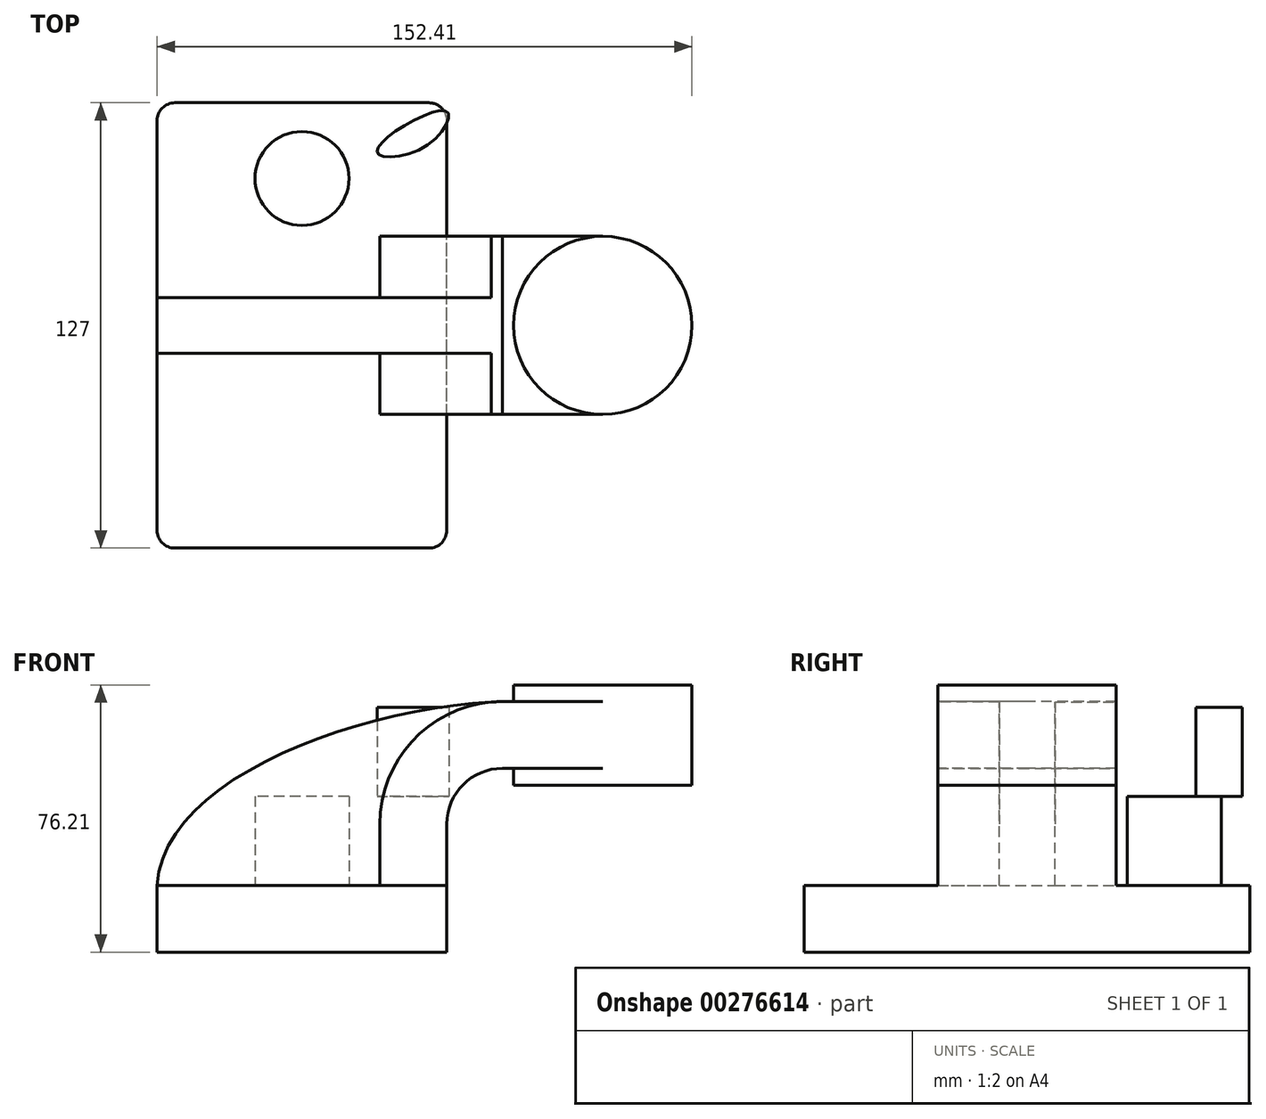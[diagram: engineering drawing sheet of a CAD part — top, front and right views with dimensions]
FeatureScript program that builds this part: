
annotation { "Feature Type Name" : "Feature", "Feature Type Description" : "" }
export const myFeature = defineFeature(function(context is Context, id is Id, definition is map)
    precondition{}
    {
        {
            var Q0;
            Q0=qCreatedBy(makeId("Front.planeOp"),FACE);
            var sketch = newSketch(context, id + "F0", { "sketchPlane" : qUnion([Q0])});
            skLineSegment(sketch, "E0.rect.bottom", {"start": v(-41.28, 9.52) * mm, "end": v(41.28, 9.52) * mm});
            skLineSegment(sketch, "E0.rect.top", {"start": v(-41.28, -9.52) * mm, "end": v(41.28, -9.52) * mm});
            skLineSegment(sketch, "E0.rect.left", {"start": v(-41.28, 9.52) * mm, "end": v(-41.28, -9.52) * mm});
            skLineSegment(sketch, "E0.rect.right", {"start": v(41.28, 9.52) * mm, "end": v(41.28, -9.52) * mm});
            skPoint(sketch, "E0.rect.middle", {"position": v(0, 0) * mm});
            skLineSegment(sketch, "E1", {"start": v(41.28, 9.52) * mm, "end": v(41.28, 27) * mm});
            skArc(sketch, "E2", {"start": v(41.28, 27) * mm, "mid": v(45.92, 38.23) * mm, "end": v(57.15, 42.88) * mm});
            skLineSegment(sketch, "E3", {"start": v(57.15, 42.88) * mm, "end": v(85.72, 42.88) * mm});
            skLineSegment(sketch, "E4.rect.bottom", {"start": v(60.32, 38.1) * mm, "end": v(111.12, 38.1) * mm});
            skLineSegment(sketch, "E4.rect.top", {"start": v(60.32, 66.68) * mm, "end": v(111.12, 66.68) * mm});
            skLineSegment(sketch, "E4.rect.left", {"start": v(60.32, 38.1) * mm, "end": v(60.32, 66.68) * mm});
            skLineSegment(sketch, "E4.rect.right", {"start": v(111.13, 38.1) * mm, "end": v(111.12, 66.68) * mm});
            skPoint(sketch, "E4.rect.middle", {"position": v(85.72, 52.39) * mm});
            skLineSegment(sketch, "E5.0", {"start": v(57.15, 61.93) * mm, "end": v(85.72, 61.93) * mm});
            skArc(sketch, "E5.1", {"start": v(22.23, 27) * mm, "mid": v(32.45, 51.7) * mm, "end": v(57.15, 61.93) * mm});
            skLineSegment(sketch, "E5.2", {"start": v(22.23, 9.52) * mm, "end": v(22.23, 27) * mm});
            skLineSegment(sketch, "E6", {"start": v(85.72, 38.1) * mm, "end": v(85.72, 66.68) * mm});
            skFitSpline(sketch, "E7", {"points": [v(-41.28, 9.53) * mm, v(57.15, 61.93) * mm], "startDerivative": vector(5.2, 92.34) * mm, "endDerivative": vector(120.92, 4.22) * mm});
            skSolve(sketch);
        }
        {
            var Q0;
            Q0=makeQuery(id+"F0.imprint","IMPRINT",FACE,{"disambiguationData":[TD([[makeQuery(id+"F0.imprint","IMPRINT",EDGE,{"derivedFrom":sQuery(id+"F0.wireOp",EDGE,"E0.rect.top")}),1.0]])]});
            extrude(context, id + "F1", {"entities" : qUnion([Q0]), "endBound" : BoundingType.SYMMETRIC, "depth" : 127 * mm});
        }
        {
            var Q0;
            {var subQ9=sQuery(id+"F0.wireOp",EDGE,"E1");Q0=makeQuery(id+"F0.imprint","IMPRINT",FACE,{"disambiguationData":[TD([[makeQuery(id+"F0.imprint","IMPRINT",EDGE,{"derivedFrom":subQ9}),1.0]])]});}
            var Q1;
            {var subQ0=sQuery(id+"F0.wireOp",EDGE,"E6");var subQ1=sQuery(id+"F0.wireOp",EDGE,"E3");var subQ2=makeQuery(id+"F0.imprint","INTERSECT",VERTEX,{"derivedFrom":[subQ1,subQ0]});Q1=makeQuery(id+"F0.imprint","IMPRINT",FACE,{"disambiguationData":[TD([[makeQuery(id+"F0.imprint","IMPRINT",EDGE,{"disambiguationData":[TD([[subQ2,1.0]])],"derivedFrom":subQ1}),1.0]])]});}
            extrude(context, id + "F2", {"entities" : qUnion([Q0, Q1]), "operationType" : NewBodyOperationType.ADD, "endBound" : BoundingType.SYMMETRIC, "depth" : 50.8 * mm});
        }
        {
            var Q0;
            {var subQ3=sQuery(id+"F0.wireOp",EDGE,"E5.2");Q0=makeQuery(id+"F0.imprint","IMPRINT",FACE,{"disambiguationData":[TD([[makeQuery(id+"F0.imprint","IMPRINT",EDGE,{"derivedFrom":subQ3}),1.0]])]});}
            extrude(context, id + "F3", {"entities" : qUnion([Q0]), "operationType" : NewBodyOperationType.ADD, "endBound" : BoundingType.SYMMETRIC, "depth" : 15.88 * mm});
        }
        {
            var Q0;
            {var subQ5=sQuery(id+"F0.wireOp",EDGE,"E4.rect.right");Q0=makeQuery(id+"F0.imprint","IMPRINT",FACE,{"disambiguationData":[TD([[makeQuery(id+"F0.imprint","IMPRINT",EDGE,{"derivedFrom":subQ5}),1.0]])]});}
            var Q1;
            Q1=sQuery(id+"F0.wireOp",EDGE,"E6");
            revolve(context, id + "F4", {"operationType" : NewBodyOperationType.ADD, "entities" : qUnion([Q0]), "axis" : qUnion([Q1]), "revolveType" : RevolveType.FULL});
        }
        {
            var Q0;
            Q0=makeQuery(id+"F1.opExtrude","CAP_EDGE",EDGE,{"disambiguationData":[OSD([sQuery(id+"F0.wireOp",EDGE,"E0.rect.right")])],"isStart":false});
            var Q1;
            Q1=makeQuery(id+"F1.opExtrude","CAP_EDGE",EDGE,{"disambiguationData":[OSD([sQuery(id+"F0.wireOp",EDGE,"E0.rect.left")])],"isStart":false});
            var Q2;
            Q2=makeQuery(id+"F1.opExtrude","CAP_EDGE",EDGE,{"disambiguationData":[OSD([sQuery(id+"F0.wireOp",EDGE,"E0.rect.right")])],"isStart":true});
            var Q3;
            Q3=makeQuery(id+"F1.opExtrude","CAP_EDGE",EDGE,{"disambiguationData":[OSD([sQuery(id+"F0.wireOp",EDGE,"E0.rect.left")])],"isStart":true});
            fillet(context, id + "F5", {"entities" : qUnion([Q0, Q1, Q2, Q3]), "radius" : 5.08 * mm, "tangentPropagation" : true, "allowEdgeOverflow" : false});
        }
        {
            var Q0;
            {var subQ4=sQuery(id+"F0.wireOp",EDGE,"E0.rect.bottom");var subQ5=sQuery(id+"F0.wireOp",EDGE,"E0.rect.right");var subQ6=sQuery(id+"F0.wireOp",EDGE,"E0.rect.left");Q0=makeQuery(id+"F3.boolean.opBoolean","SPLIT",FACE,{"disambiguationData":[TD([makeQuery(id+"F1.opExtrude","CAP_FACE",FACE,{"disambiguationData":[OSD([subQ4,sQuery(id+"F0.wireOp",EDGE,"E0.rect.top"),subQ6,subQ5])],"isStart":true})])],"derivedFrom":makeQuery(id+"F1.opExtrude","SWEPT_FACE",FACE,{"disambiguationData":[OSD([subQ4])]})});}
            var sketch = newSketch(context, id + "F6", { "sketchPlane" : qUnion([Q0])});
            skCircle(sketch, "E8", {"center": v(0, 41.91) * mm, "radius": 13.38 * mm});
            skPoint(sketch, "E8.centerSnap0", {"position": v(41.28, 41.91) * mm});
            skSolve(sketch);
        }
        {
            var Q0;
            Q0=makeQuery(id+"F6.imprint","IMPRINT",FACE,{"disambiguationData":[TD([[makeQuery(id+"F6.imprint","IMPRINT",EDGE,{"derivedFrom":sQuery(id+"F6.wireOp",EDGE,"E8")}),1.0]])]});
            extrude(context, id + "F7", {"entities" : qUnion([Q0]), "operationType" : NewBodyOperationType.ADD, "depth" : 25.4 * mm});
        }
        {
            var Q0;
            Q0=makeQuery(id+"F7.opExtrude","CAP_FACE",FACE,{"disambiguationData":[OSD([sQuery(id+"F6.wireOp",EDGE,"E8")])],"isStart":false});
            var sketch = newSketch(context, id + "F8", { "sketchPlane" : qUnion([Q0])});
            skFitSpline(sketch, "E9", {"points": [v(35.81, 51.46) * mm, v(41.4, 60.88) * mm, v(26.51, 55.26) * mm, v(21.67, 48.93) * mm, v(35.81, 51.46) * mm]});
            skSolve(sketch);
        }
        {
            var Q0;
            Q0=makeQuery(id+"F8.imprint","IMPRINT",FACE,{"disambiguationData":[TD([[makeQuery(id+"F8.imprint","IMPRINT",EDGE,{"derivedFrom":sQuery(id+"F8.wireOp",EDGE,"E9")}),1.0]])]});
            extrude(context, id + "F9", {"entities" : qUnion([Q0]), "depth" : 25.4 * mm});
        }
    });
